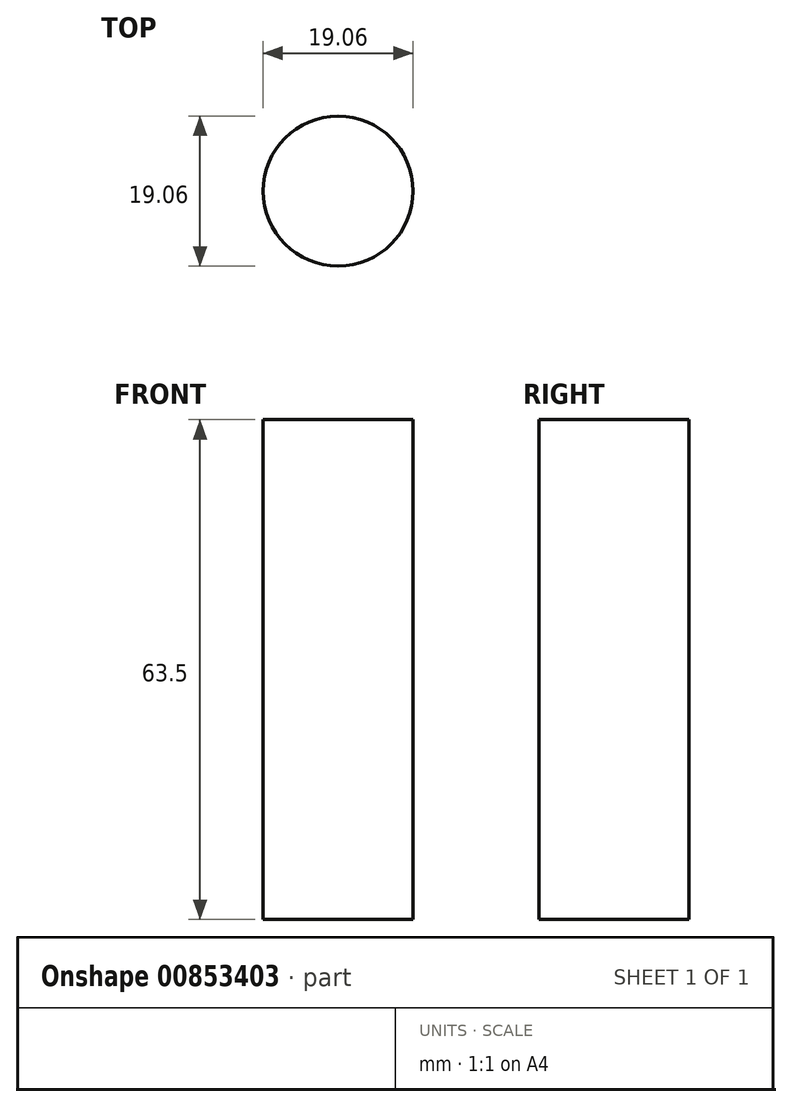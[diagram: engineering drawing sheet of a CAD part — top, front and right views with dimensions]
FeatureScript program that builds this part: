
annotation { "Feature Type Name" : "Feature", "Feature Type Description" : "" }
export const myFeature = defineFeature(function(context is Context, id is Id, definition is map)
    precondition{}
    {
        {
            var Q0;
            Q0=qCreatedBy(makeId("Top.planeOp"),FACE);
            var sketch = newSketch(context, id + "F0", { "sketchPlane" : qUnion([Q0])});
            skCircle(sketch, "E0", {"center": v(0, 0) * mm, "radius": 9.52 * mm});
            skSolve(sketch);
        }
        {
            var Q0;
            Q0 = qSketchRegion(id + "F0", true);
            extrude(context, id + "F1", {"entities" : qUnion([Q0]), "depth" : 63.5 * mm, "offsetDistance" : 25.4 * mm});
        }
    });
